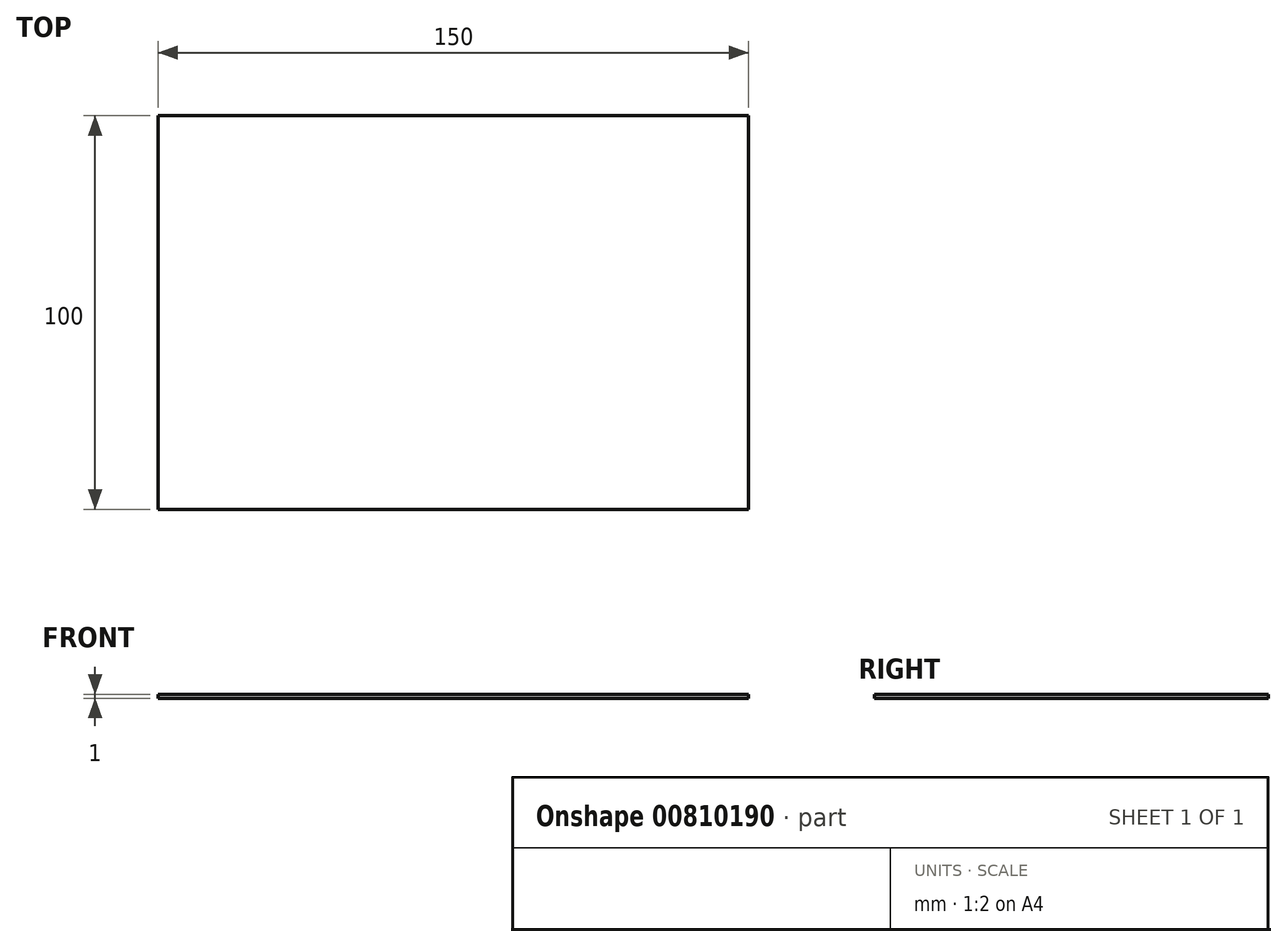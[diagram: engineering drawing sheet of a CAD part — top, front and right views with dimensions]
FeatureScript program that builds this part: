
annotation { "Feature Type Name" : "Feature", "Feature Type Description" : "" }
export const myFeature = defineFeature(function(context is Context, id is Id, definition is map)
    precondition{}
    {
        {
            var Q0;
            Q0=qCreatedBy(makeId("Top.planeOp"),FACE);
            var sketch = newSketch(context, id + "F0", { "sketchPlane" : qUnion([Q0])});
            skLineSegment(sketch, "E0.bottom", {"start": v(-75, 50) * mm, "end": v(75, 50) * mm});
            skLineSegment(sketch, "E0.top", {"start": v(-75, -50) * mm, "end": v(75, -50) * mm});
            skLineSegment(sketch, "E0.left", {"start": v(-75, 50) * mm, "end": v(-75, -50) * mm});
            skLineSegment(sketch, "E0.right", {"start": v(75, 50) * mm, "end": v(75, -50) * mm});
            skPoint(sketch, "E0.middle", {"position": v(0, 0) * mm});
            skSolve(sketch);
        }
        {
            var Q0;
            Q0 = qSketchRegion(id + "F0", true);
            extrude(context, id + "F1", {"entities" : qUnion([Q0]), "depth" : 1 * mm, "offsetDistance" : 25 * mm});
        }
    });
